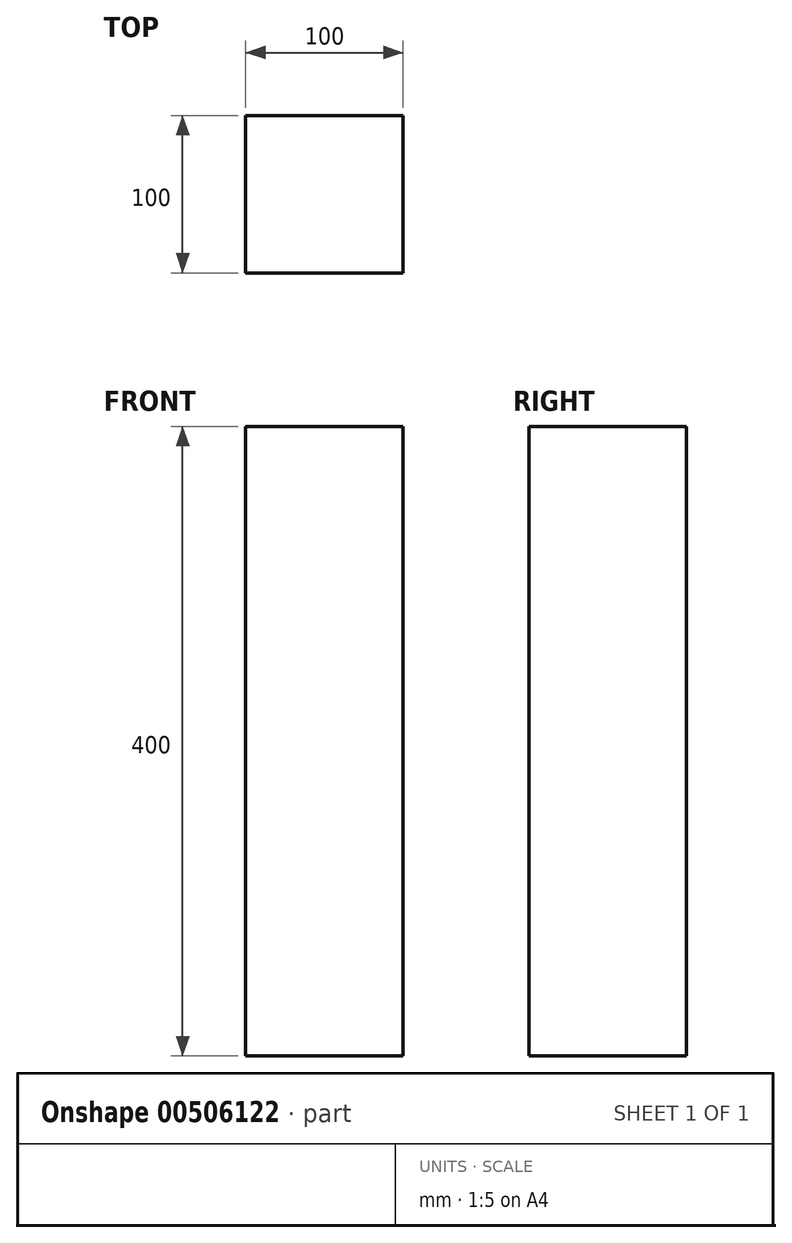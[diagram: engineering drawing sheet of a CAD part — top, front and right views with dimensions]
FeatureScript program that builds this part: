
annotation { "Feature Type Name" : "Feature", "Feature Type Description" : "" }
export const myFeature = defineFeature(function(context is Context, id is Id, definition is map)
    precondition{}
    {
        {
            var Q0;
            Q0=qCreatedBy(makeId("Top.planeOp"),FACE);
            var sketch = newSketch(context, id + "F0", { "sketchPlane" : qUnion([Q0])});
            skLineSegment(sketch, "E0.bottom", {"start": v(50, -50) * mm, "end": v(-50, -50) * mm});
            skLineSegment(sketch, "E0.top", {"start": v(50, 50) * mm, "end": v(-50, 50) * mm});
            skLineSegment(sketch, "E0.left", {"start": v(50, -50) * mm, "end": v(50, 50) * mm});
            skLineSegment(sketch, "E0.right", {"start": v(-50, -50) * mm, "end": v(-50, 50) * mm});
            skPoint(sketch, "E0.middle", {"position": v(0, 0) * mm});
            skSolve(sketch);
        }
        {
            var Q0;
            Q0 = qSketchRegion(id + "F0", true);
            extrude(context, id + "F1", {"entities" : qUnion([Q0]), "endBound" : BoundingType.SYMMETRIC, "depth" : 400 * mm});
        }
    });
